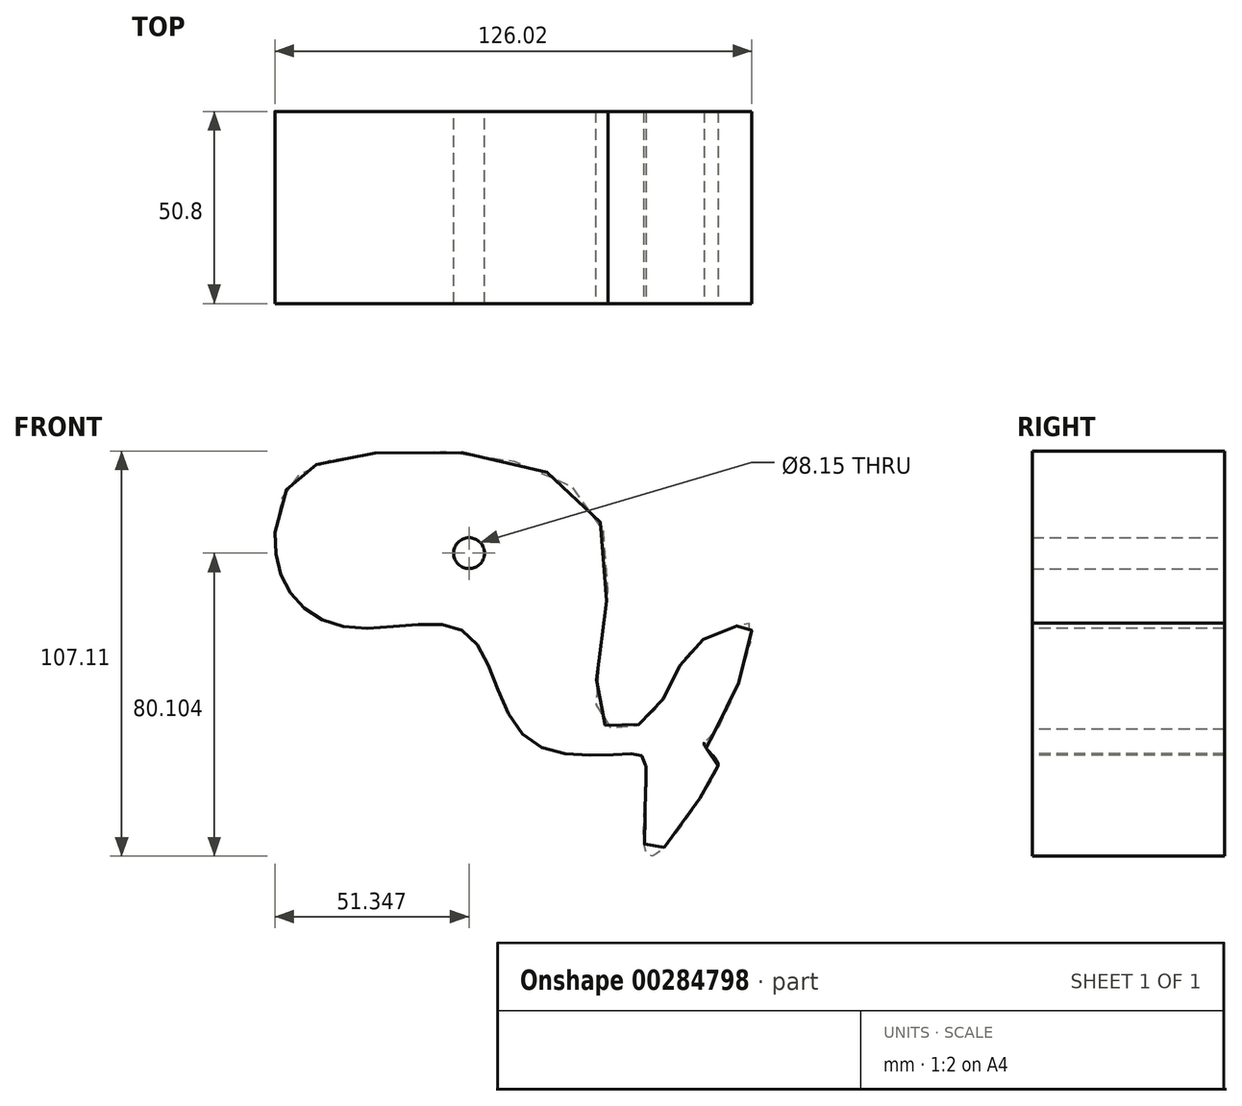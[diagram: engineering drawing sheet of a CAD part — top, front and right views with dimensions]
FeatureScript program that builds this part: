
annotation { "Feature Type Name" : "Feature", "Feature Type Description" : "" }
export const myFeature = defineFeature(function(context is Context, id is Id, definition is map)
    precondition{}
    {
        {
            var Q0;
            Q0=qCreatedBy(makeId("Front.planeOp"),FACE);
            var sketch = newSketch(context, id + "F0", { "sketchPlane" : qUnion([Q0])});
            skFitSpline(sketch, "E0", {"points": [v(-38.8, 29.1) * mm, v(25.15, 14.24) * mm, v(26.06, -40) * mm, v(36.37, -42.13) * mm, v(44.85, -31.82) * mm, v(52.13, -20.6) * mm, v(63.95, -15.46) * mm, v(66.37, -15.76) * mm, v(57.28, -43.34) * mm, v(53.95, -47.28) * mm, v(57.28, -51.52) * mm, v(55.76, -56.67) * mm, v(39.4, -76.68) * mm, v(38.49, -52.73) * mm, v(34.85, -49.7) * mm, v(7.58, -46.07) * mm, v(-8.79, -17.88) * mm, v(-39.4, -16.37) * mm, v(-57.89, -2.42) * mm, v(-56.67, 19.7) * mm, v(-38.8, 29.1) * mm]});
            skFitSpline(sketch, "E1", {"points": [v(38.49, -52.73) * mm, v(38.49, -58.6) * mm], "startDerivative": vector(0, -5.86) * mm, "endDerivative": vector(0, -5.86) * mm});
            skCircle(sketch, "E2", {"center": v(-8.18, 3.33) * mm, "radius": 4.08 * mm});
            skFitSpline(sketch, "E3", {"points": [v(-59.49, 8.8) * mm, v(-29.4, 10.6) * mm, v(-21.52, 2.73) * mm, v(-14.85, -6.06) * mm, v(0, -5.15) * mm, v(0, -3.64) * mm], "startDerivative": vector(109.95, 19.5) * mm, "endDerivative": vector(-10.19, 21.65) * mm});
            skSolve(sketch);
        }
        {
            var Q0;
            Q0=makeQuery(id+"F0.imprint","IMPRINT",FACE,{"disambiguationData":[TD([[makeQuery(id+"F0.imprint","IMPRINT",EDGE,{"derivedFrom":sQuery(id+"F0.wireOp",EDGE,"E2")}),-1.0]])]});
            extrude(context, id + "F1", {"entities" : qUnion([Q0]), "depth" : 50.8 * mm});
        }
    });
